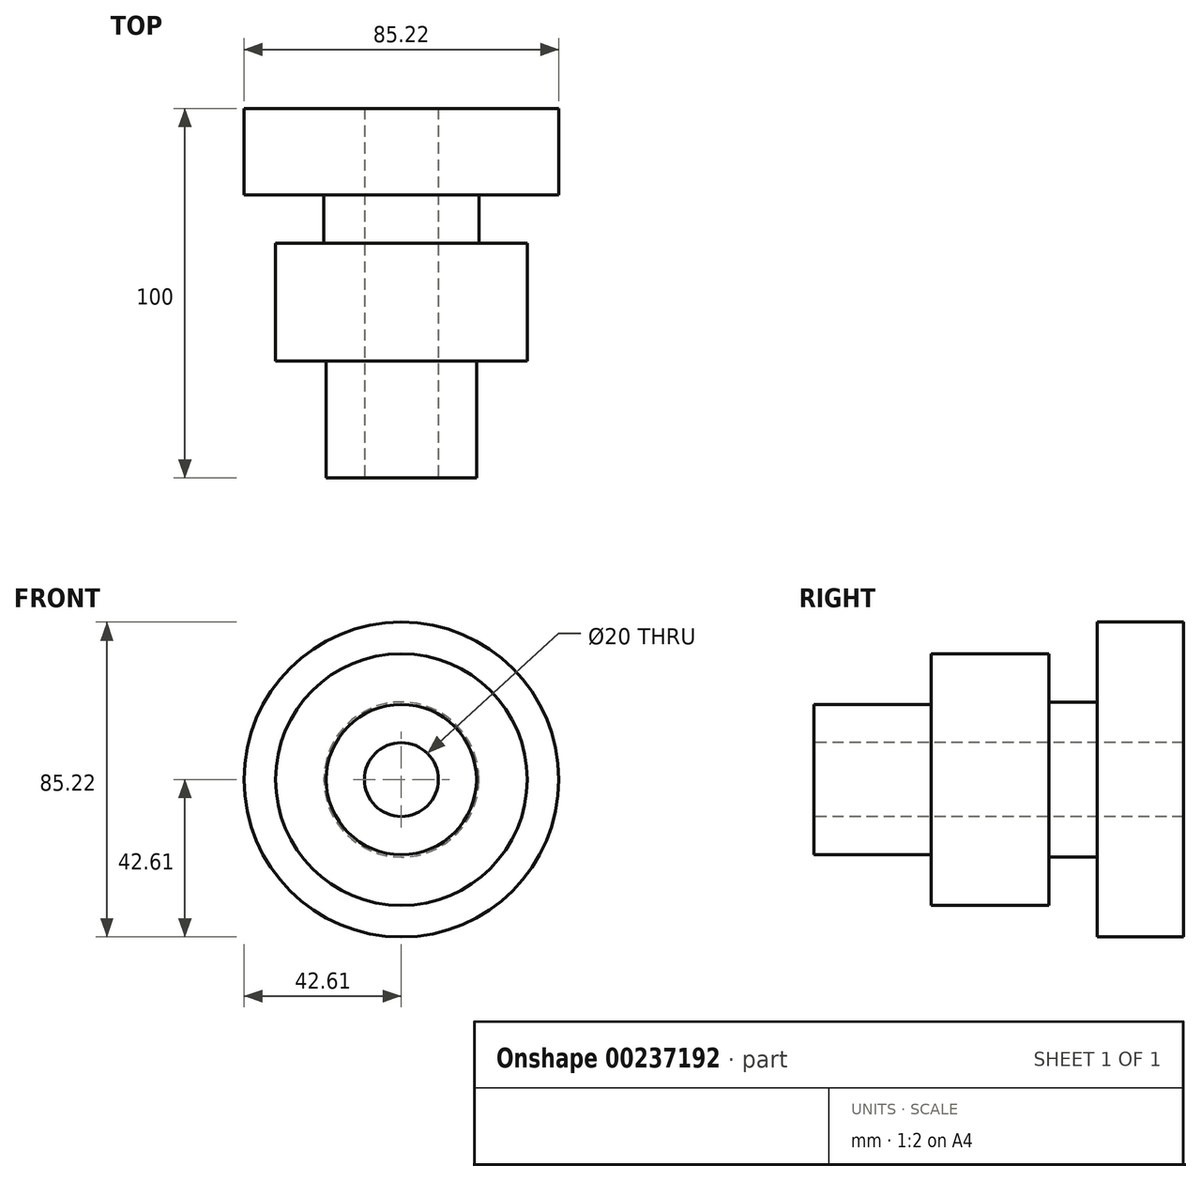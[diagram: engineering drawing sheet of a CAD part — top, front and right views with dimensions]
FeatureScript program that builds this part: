
annotation { "Feature Type Name" : "Feature", "Feature Type Description" : "" }
export const myFeature = defineFeature(function(context is Context, id is Id, definition is map)
    precondition{}
    {
        {
            var Q0;
            Q0=qCreatedBy(makeId("Right.planeOp"),FACE);
            var sketch = newSketch(context, id + "F0", { "sketchPlane" : qUnion([Q0])});
            skLineSegment(sketch, "E0", {"start": v(0, 0) * mm, "end": v(106.03, 0) * mm, "construction": true});
            skLineSegment(sketch, "E1", {"start": v(0, 10) * mm, "end": v(100, 10) * mm});
            skLineSegment(sketch, "E2", {"start": v(100, 10) * mm, "end": v(100, 42.6) * mm});
            skLineSegment(sketch, "E3", {"start": v(100, 42.6) * mm, "end": v(76.64, 42.6) * mm});
            skLineSegment(sketch, "E4", {"start": v(76.64, 42.6) * mm, "end": v(76.64, 20.98) * mm});
            skLineSegment(sketch, "E5", {"start": v(76.64, 20.98) * mm, "end": v(63.52, 20.98) * mm});
            skLineSegment(sketch, "E6", {"start": v(63.52, 20.98) * mm, "end": v(63.52, 34.06) * mm});
            skLineSegment(sketch, "E7", {"start": v(63.52, 34.06) * mm, "end": v(31.65, 34.06) * mm});
            skLineSegment(sketch, "E8", {"start": v(31.65, 34.06) * mm, "end": v(31.65, 20.34) * mm});
            skLineSegment(sketch, "E9", {"start": v(31.65, 20.34) * mm, "end": v(0, 20.34) * mm});
            skLineSegment(sketch, "E10", {"start": v(0, 20.34) * mm, "end": v(0, 10) * mm});
            skSolve(sketch);
        }
        {
            var Q0;
            Q0=makeQuery(id+"F0.imprint","IMPRINT",FACE,{"disambiguationData":[TD([[makeQuery(id+"F0.imprint","IMPRINT",EDGE,{"derivedFrom":sQuery(id+"F0.wireOp",EDGE,"E1")}),1.0]])]});
            var Q1;
            Q1=sQuery(id+"F0.wireOp",EDGE,"E0");
            revolve(context, id + "F1", {"entities" : qUnion([Q0]), "axis" : qUnion([Q1]), "revolveType" : RevolveType.FULL});
        }
    });
